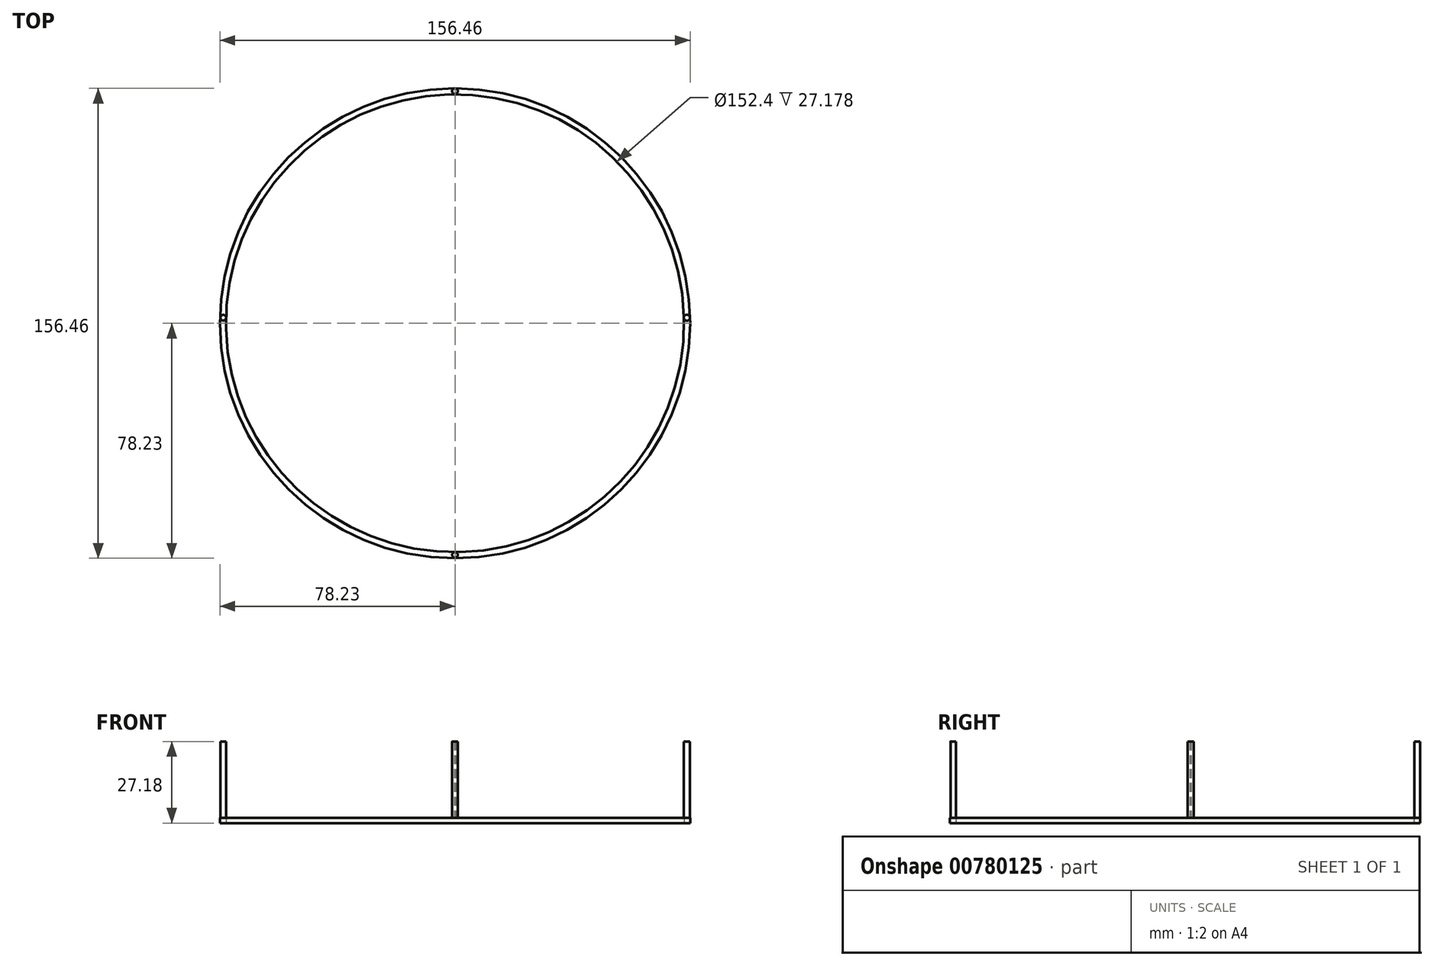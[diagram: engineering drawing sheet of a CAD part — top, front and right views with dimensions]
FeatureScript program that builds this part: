
annotation { "Feature Type Name" : "Feature", "Feature Type Description" : "" }
export const myFeature = defineFeature(function(context is Context, id is Id, definition is map)
    precondition{}
    {
        {
            var Q0;
            Q0=qCreatedBy(makeId("Top.planeOp"),FACE);
            var sketch = newSketch(context, id + "F0", { "sketchPlane" : qUnion([Q0])});
            skCircle(sketch, "E0", {"center": v(0, 0) * mm, "radius": 76.2 * mm});
            skCircle(sketch, "E1.0", {"center": v(0, 0) * mm, "radius": 78.23 * mm});
            skSolve(sketch);
        }
        {
            var Q0;
            Q0=makeQuery(id+"F0.imprint","IMPRINT",FACE,{"disambiguationData":[TD([[makeQuery(id+"F0.imprint","IMPRINT",EDGE,{"derivedFrom":sQuery(id+"F0.wireOp",EDGE,"E0")}),-1.0]])]});
            extrude(context, id + "F1", {"entities" : qUnion([Q0]), "depth" : 1.78 * mm, "offsetDistance" : 25.4 * mm});
        }
        {
            var Q0;
            Q0=makeQuery(id+"F1.opExtrude","CAP_FACE",FACE,{"disambiguationData":[OSD([sQuery(id+"F0.wireOp",EDGE,"E0"),sQuery(id+"F0.wireOp",EDGE,"E1.0")])],"isStart":false});
            var sketch = newSketch(context, id + "F2", { "sketchPlane" : qUnion([Q0])});
            skCircle(sketch, "E2", {"center": v(-77.11, 1.87) * mm, "radius": 0.93 * mm});
            skCircle(sketch, "E3", {"center": v(77.16, 1.87) * mm, "radius": 1.01 * mm});
            skCircle(sketch, "E4", {"center": v(0, 77.3) * mm, "radius": 0.95 * mm});
            skCircle(sketch, "E5", {"center": v(0, -77.13) * mm, "radius": 0.92 * mm});
            skSolve(sketch);
        }
        {
            var Q0;
            Q0=makeQuery(id+"F2.imprint","IMPRINT",FACE,{"disambiguationData":[TD([[makeQuery(id+"F2.imprint","IMPRINT",EDGE,{"derivedFrom":sQuery(id+"F2.wireOp",EDGE,"E2")}),1.0]])]});
            var Q1;
            {var subQ0=sQuery(id+"F2.wireOp",EDGE,"E3");var subQ1=makeQuery(id+"F1.opExtrude","CAP_EDGE",EDGE,{"disambiguationData":[OSD([sQuery(id+"F0.wireOp",EDGE,"E0")])],"isStart":false});var subQ2=makeQuery(id+"F2.imprint","INTERSECT",VERTEX,{"disambiguationData":[OD(0.0)],"derivedFrom":[subQ1,subQ0]});Q1=makeQuery(id+"F2.imprint","IMPRINT",FACE,{"disambiguationData":[TD([[makeQuery(id+"F2.imprint","IMPRINT",EDGE,{"disambiguationData":[TD([[subQ2,-1.0]])],"derivedFrom":subQ0}),1.0]])]});}
            var Q2;
            Q2=makeQuery(id+"F2.imprint","IMPRINT",FACE,{"disambiguationData":[TD([[makeQuery(id+"F2.imprint","IMPRINT",EDGE,{"derivedFrom":sQuery(id+"F2.wireOp",EDGE,"E5")}),1.0]])]});
            var Q3;
            {var subQ0=sQuery(id+"F2.wireOp",EDGE,"E4");var subQ1=makeQuery(id+"F1.opExtrude","CAP_EDGE",EDGE,{"disambiguationData":[OSD([sQuery(id+"F0.wireOp",EDGE,"E1.0")])],"isStart":false});var subQ2=makeQuery(id+"F2.imprint","INTERSECT",VERTEX,{"disambiguationData":[OD(0.0)],"derivedFrom":[subQ1,subQ0]});Q3=makeQuery(id+"F2.imprint","IMPRINT",FACE,{"disambiguationData":[TD([[makeQuery(id+"F2.imprint","IMPRINT",EDGE,{"disambiguationData":[TD([[subQ2,-1.0]])],"derivedFrom":subQ0}),1.0]])]});}
            extrude(context, id + "F3", {"entities" : qUnion([Q0, Q1, Q2, Q3]), "operationType" : NewBodyOperationType.ADD, "depth" : 25.4 * mm, "offsetDistance" : 25.4 * mm});
        }
    });
